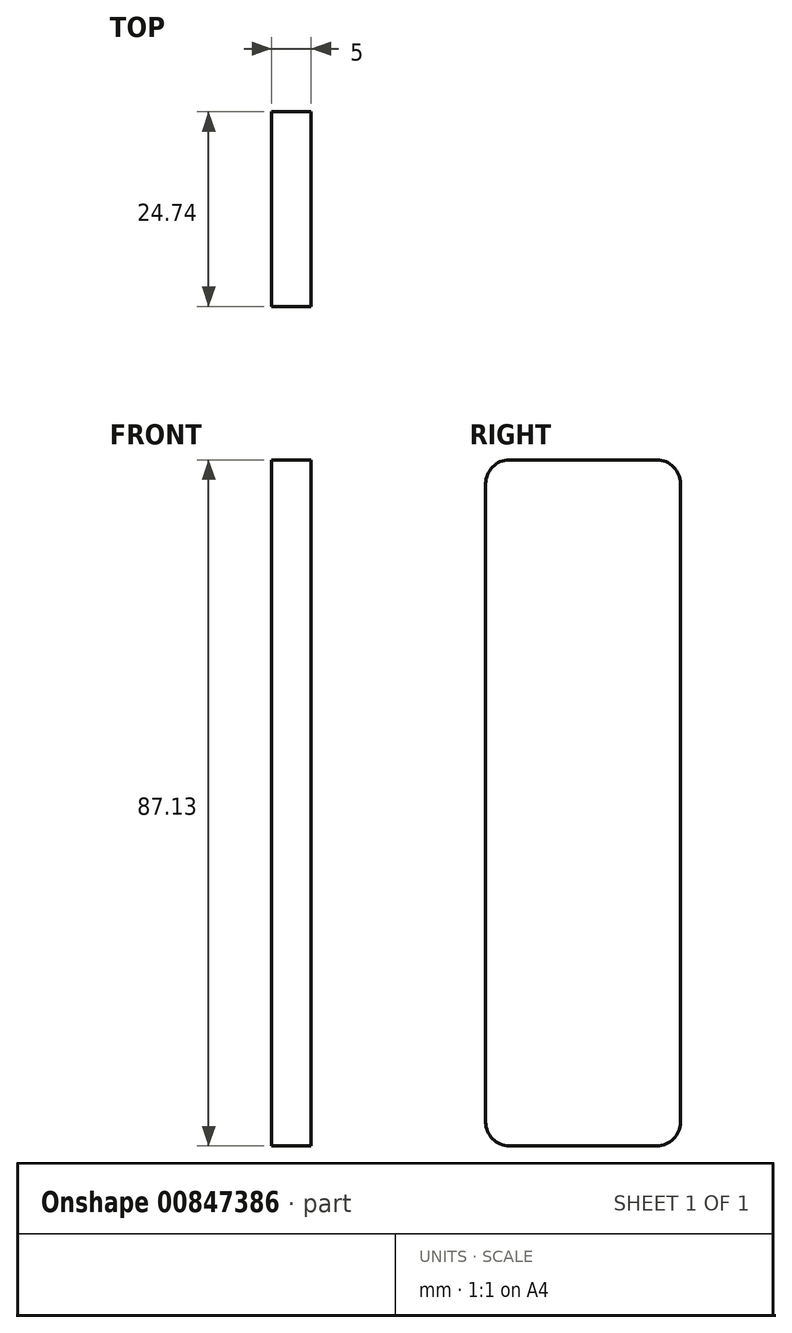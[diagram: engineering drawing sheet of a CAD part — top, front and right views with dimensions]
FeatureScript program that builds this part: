
annotation { "Feature Type Name" : "Feature", "Feature Type Description" : "" }
export const myFeature = defineFeature(function(context is Context, id is Id, definition is map)
    precondition{}
    {
        {
            var Q0;
            Q0=qCreatedBy(makeId("Right.planeOp"),FACE);
            var sketch = newSketch(context, id + "F0", { "sketchPlane" : qUnion([Q0])});
            skLineSegment(sketch, "E0.bottom", {"start": v(-52.18, 46.93) * mm, "end": v(-33.44, 46.93) * mm});
            skLineSegment(sketch, "E0.top", {"start": v(-52.18, -40.2) * mm, "end": v(-33.44, -40.2) * mm});
            skLineSegment(sketch, "E0.left", {"start": v(-55.18, 43.93) * mm, "end": v(-55.18, -37.2) * mm});
            skLineSegment(sketch, "E0.right", {"start": v(-30.44, 43.93) * mm, "end": v(-30.44, -37.2) * mm});
            skPoint(sketch, "E1.visualSharp", {"position": v(-55.18, 46.93) * mm});
            skArc(sketch, "E1.filletArc", {"start": v(-52.18, 46.93) * mm, "mid": v(-54.3, 46.06) * mm, "end": v(-55.18, 43.93) * mm});
            skPoint(sketch, "E2.visualSharp", {"position": v(-30.44, 46.93) * mm});
            skArc(sketch, "E2.filletArc", {"start": v(-30.44, 43.93) * mm, "mid": v(-31.32, 46.06) * mm, "end": v(-33.44, 46.93) * mm});
            skPoint(sketch, "E3.visualSharp", {"position": v(-30.44, -40.2) * mm});
            skArc(sketch, "E3.filletArc", {"start": v(-33.44, -40.2) * mm, "mid": v(-31.32, -39.32) * mm, "end": v(-30.44, -37.2) * mm});
            skPoint(sketch, "E4.visualSharp", {"position": v(-55.18, -40.2) * mm});
            skArc(sketch, "E4.filletArc", {"start": v(-55.18, -37.2) * mm, "mid": v(-54.3, -39.32) * mm, "end": v(-52.18, -40.2) * mm});
            skSolve(sketch);
        }
        {
            var Q0;
            Q0=makeQuery(id+"F0.imprint","IMPRINT",FACE,{"disambiguationData":[TD([[makeQuery(id+"F0.imprint","IMPRINT",EDGE,{"derivedFrom":sQuery(id+"F0.wireOp",EDGE,"E0.bottom")}),-1.0]])]});
            extrude(context, id + "F1", {"entities" : qUnion([Q0]), "depth" : 5 * mm, "offsetDistance" : 25 * mm});
        }
    });
